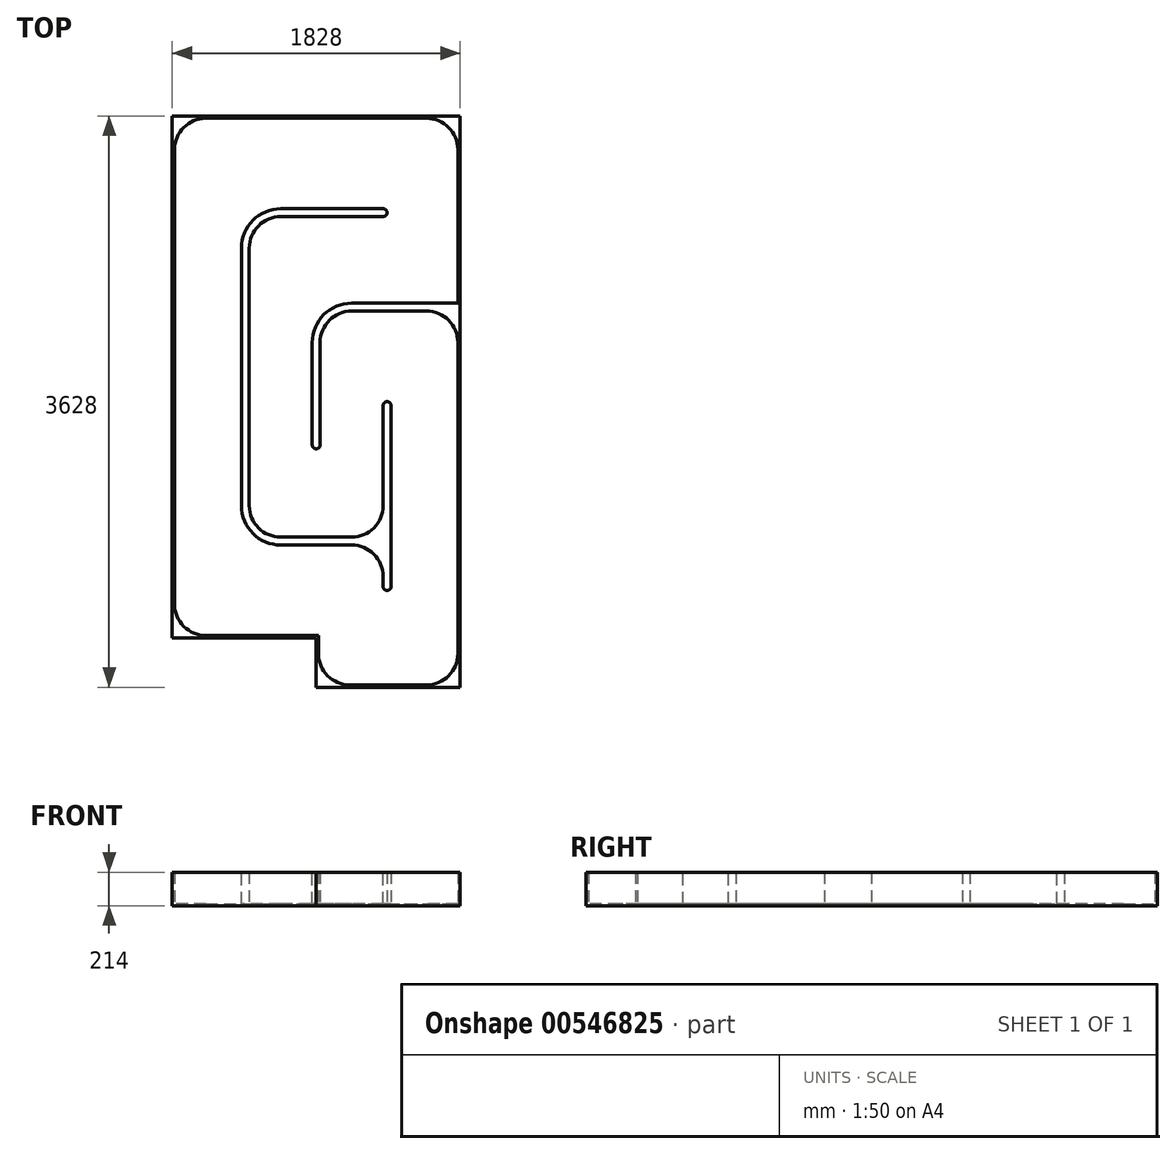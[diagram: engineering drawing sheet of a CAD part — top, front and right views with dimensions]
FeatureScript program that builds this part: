
annotation { "Feature Type Name" : "Feature", "Feature Type Description" : "" }
export const myFeature = defineFeature(function(context is Context, id is Id, definition is map)
    precondition{}
    {
        {
            assignVariable(context, id + "F0", {"name" : "H", "anyValue" : 200});
        }
        {
            assignVariable(context, id + "F1", {"name" : "t", "anyValue" : 14});
        }
        {
            assignVariable(context, id + "F2", {"name" : "w2", "anyValue" : 50});
        }
        {
            assignVariable(context, id + "F3", {"name" : "R1", "anyValue" : 200});
        }
        {
            assignVariable(context, id + "F4", {"name" : "R2", "anyValue" : getVariable(context, 'w2') / 2});
        }
        {
            var Q0;
            Q0=qCreatedBy(makeId("Top.planeOp"),FACE);
            var sketch = newSketch(context, id + "F5", { "sketchPlane" : qUnion([Q0])});
            skPoint(sketch, "E0.middle", {"position": v(0, 0) * mm});
            skLineSegment(sketch, "E1.bottom", {"start": v(-914, 1814) * mm, "end": v(914, 1814) * mm});
            skLineSegment(sketch, "E1.top", {"start": v(0, -1814) * mm, "end": v(914, -1814) * mm});
            skLineSegment(sketch, "E1.left", {"start": v(-914, 1814) * mm, "end": v(-914, -1500) * mm});
            skLineSegment(sketch, "E1.right", {"start": v(914, 1814) * mm, "end": v(914, -1814) * mm});
            skLineSegment(sketch, "E2", {"start": v(-914, -1500) * mm, "end": v(0, -1500) * mm});
            skLineSegment(sketch, "E3", {"start": v(0, -1500) * mm, "end": v(0, -1814) * mm});
            skPoint(sketch, "E4.orphan", {"position": v(-914, -1814) * mm});
            skPoint(sketch, "E5.orphan", {"position": v(914, -1814) * mm});
            skSolve(sketch);
        }
        {
            var Q0;
            Q0 = qSketchRegion(id + "F5", true);
            extrude(context, id + "F6", {"entities" : qUnion([Q0]), "depth" : (getVariable(context, 'H')) * mm, "offsetDistance" : 25 * mm, "hasSecondDirection" : true, "secondDirectionOppositeDirection" : true, "secondDirectionDepth" : (getVariable(context, 't')) * mm});
        }
        {
            var Q0;
            Q0=makeQuery(id+"F6.opExtrude","CAP_FACE",FACE,{"disambiguationData":[OSD([sQuery(id+"F5.wireOp",EDGE,"E1.bottom"),sQuery(id+"F5.wireOp",EDGE,"E1.top"),sQuery(id+"F5.wireOp",EDGE,"E1.left"),sQuery(id+"F5.wireOp",EDGE,"E1.right"),sQuery(id+"F5.wireOp",EDGE,"E2"),sQuery(id+"F5.wireOp",EDGE,"E3")])],"isStart":false});
            shell(context, id + "F7", {"entities" : qUnion([Q0]), "thickness" : (getVariable(context, 't')) * mm});
        }
        {
            var Q0;
            Q0=qCreatedBy(makeId("Top.planeOp"),FACE);
            var sketch = newSketch(context, id + "F8", { "sketchPlane" : qUnion([Q0])});
            skLineSegment(sketch, "E6", {"start": v(450, 1200) * mm, "end": v(-450, 1200) * mm});
            skLineSegment(sketch, "E7", {"start": v(-450, 1200) * mm, "end": v(-450, -886) * mm});
            skLineSegment(sketch, "E8", {"start": v(-450, -886) * mm, "end": v(450, -886) * mm});
            skLineSegment(sketch, "E9", {"start": v(450, -1200) * mm, "end": v(450, 0) * mm});
            skLineSegment(sketch, "E10", {"start": v(0, -300) * mm, "end": v(0, 600) * mm});
            skLineSegment(sketch, "E11", {"start": v(0, 600) * mm, "end": v(900, 600) * mm});
            skPoint(sketch, "E12.orphan", {"position": v(900, 1800) * mm});
            skSolve(sketch);
        }
        {
            var Q0;
            Q0=qCreatedBy(makeId("Right.planeOp"),FACE);
            var Q1;
            Q1=sQuery(id+"F8.wireOp",VERTEX,"E6.start");
            cPlane(context, id + "F9", {"entities" : qUnion([Q0, Q1]), "cplaneType" : CPlaneType.PLANE_POINT, "offset" : 25 * mm, "width" : 150 * mm, "height" : 150 * mm});
        }
        {
            var Q0;
            Q0=qCreatedBy(makeId("Front.planeOp"),FACE);
            var Q1;
            Q1=sQuery(id+"F8.wireOp",VERTEX,"E9.start");
            cPlane(context, id + "F10", {"entities" : qUnion([Q0, Q1]), "cplaneType" : CPlaneType.PLANE_POINT, "offset" : 25 * mm, "width" : 150 * mm, "height" : 150 * mm});
        }
        {
            var Q0;
            Q0=qCreatedBy(makeId("Front.planeOp"),FACE);
            var Q1;
            Q1=sQuery(id+"F8.wireOp",VERTEX,"E10.start");
            cPlane(context, id + "F11", {"entities" : qUnion([Q0, Q1]), "cplaneType" : CPlaneType.PLANE_POINT, "offset" : 25 * mm, "width" : 150 * mm, "height" : 150 * mm});
        }
        {
            var Q0;
            Q0=qCreatedBy(id+"F9.planeOp",FACE);
            var sketch = newSketch(context, id + "F12", { "sketchPlane" : qUnion([Q0])});
            skPoint(sketch, "E13.0", {"position": v(1200, 0) * mm});
            skLineSegment(sketch, "E14.bottom", {"start": v(1175, 200) * mm, "end": v(1225, 200) * mm});
            skLineSegment(sketch, "E14.top", {"start": v(1175, 0) * mm, "end": v(1225, 0) * mm});
            skLineSegment(sketch, "E14.left", {"start": v(1175, 200) * mm, "end": v(1175, 0) * mm});
            skLineSegment(sketch, "E14.right", {"start": v(1225, 200) * mm, "end": v(1225, 0) * mm});
            skSolve(sketch);
        }
        {
            var Q0;
            Q0=qCreatedBy(id+"F10.planeOp",FACE);
            var sketch = newSketch(context, id + "F13", { "sketchPlane" : qUnion([Q0])});
            skPoint(sketch, "E15.0", {"position": v(450, 0) * mm});
            skLineSegment(sketch, "E16.bottom", {"start": v(425, 200) * mm, "end": v(475, 200) * mm});
            skLineSegment(sketch, "E16.top", {"start": v(425, 0) * mm, "end": v(475, 0) * mm});
            skLineSegment(sketch, "E16.left", {"start": v(425, 200) * mm, "end": v(425, 0) * mm});
            skLineSegment(sketch, "E16.right", {"start": v(475, 200) * mm, "end": v(475, 0) * mm});
            skSolve(sketch);
        }
        {
            var Q0;
            Q0=qCreatedBy(id+"F11.planeOp",FACE);
            var sketch = newSketch(context, id + "F14", { "sketchPlane" : qUnion([Q0])});
            skLineSegment(sketch, "E17.bottom", {"start": v(-25, 200) * mm, "end": v(25, 200) * mm});
            skLineSegment(sketch, "E17.top", {"start": v(-25, 0) * mm, "end": v(25, 0) * mm});
            skLineSegment(sketch, "E17.left", {"start": v(-25, 200) * mm, "end": v(-25, 0) * mm});
            skLineSegment(sketch, "E17.right", {"start": v(25, 200) * mm, "end": v(25, 0) * mm});
            skSolve(sketch);
        }
        {
            var Q0;
            Q0 = qSketchRegion(id + "F12", true);
            var Q1;
            Q1=sQuery(id+"F8.wireOp",EDGE,"E6");
            var Q2;
            Q2=sQuery(id+"F8.wireOp",EDGE,"E7");
            var Q3;
            Q3=sQuery(id+"F8.wireOp",EDGE,"E8");
            sweep(context, id + "F15", {"profiles" : qUnion([Q0]), "path" : qUnion([Q1, Q2, Q3])});
        }
        {
            var Q0;
            Q0 = qSketchRegion(id + "F13", true);
            var Q1;
            Q1=sQuery(id+"F8.wireOp",EDGE,"E9");
            sweep(context, id + "F16", {"profiles" : qUnion([Q0]), "path" : qUnion([Q1])});
        }
        {
            var Q0;
            Q0 = qSketchRegion(id + "F14", true);
            var Q1;
            Q1=sQuery(id+"F8.wireOp",EDGE,"E10");
            var Q2;
            Q2=sQuery(id+"F8.wireOp",EDGE,"E11");
            sweep(context, id + "F17", {"operationType" : NewBodyOperationType.ADD, "profiles" : qUnion([Q0]), "path" : qUnion([Q1, Q2])});
        }
        {
            var Q0;
            Q0=makeQuery(id+"F15.opSweep","SWEPT_BODY",BODY,{"disambiguationData":[OSD([sQuery(id+"F8.wireOp",EDGE,"E8"),sQuery(id+"F12.wireOp",EDGE,"E14.bottom"),sQuery(id+"F12.wireOp",EDGE,"E14.top"),sQuery(id+"F12.wireOp",EDGE,"E14.left"),sQuery(id+"F12.wireOp",EDGE,"E14.right")])]});
            var Q1;
            Q1=makeQuery(id+"F16.opSweep","SWEPT_BODY",BODY,{"disambiguationData":[OSD([sQuery(id+"F8.wireOp",EDGE,"E9"),sQuery(id+"F13.wireOp",EDGE,"E16.bottom"),sQuery(id+"F13.wireOp",EDGE,"E16.top"),sQuery(id+"F13.wireOp",EDGE,"E16.left"),sQuery(id+"F13.wireOp",EDGE,"E16.right")])]});
            booleanBodies(context, id + "F18", {"operationType" : BooleanOperationType.UNION, "tools" : qUnion([Q0, Q1])});
        }
        {
            var Q0;
            Q0=makeQuery(id+"F18.opBoolean","INTERSECT",EDGE,{"derivedFrom":[makeQuery(id+"F15.opSweep","SWEPT_FACE",FACE,{"disambiguationData":[OSD([sQuery(id+"F8.wireOp",EDGE,"E8"),sQuery(id+"F12.wireOp",EDGE,"E14.right")])]}),makeQuery(id+"F16.opSweep","SWEPT_FACE",FACE,{"disambiguationData":[OSD([sQuery(id+"F8.wireOp",EDGE,"E9"),sQuery(id+"F13.wireOp",EDGE,"E16.left")])]})]});
            var Q1;
            Q1=makeQuery(id+"F18.opBoolean","INTERSECT",EDGE,{"derivedFrom":[makeQuery(id+"F15.opSweep","SWEPT_FACE",FACE,{"disambiguationData":[OSD([sQuery(id+"F8.wireOp",EDGE,"E8"),sQuery(id+"F12.wireOp",EDGE,"E14.left")])]}),makeQuery(id+"F16.opSweep","SWEPT_FACE",FACE,{"disambiguationData":[OSD([sQuery(id+"F8.wireOp",EDGE,"E9"),sQuery(id+"F13.wireOp",EDGE,"E16.left")])]})]});
            var Q2;
            Q2=makeQuery(id+"F15.opSweep","MID_CAP_EDGE",EDGE,{"disambiguationData":[OSD([sQuery(id+"F8.wireOp",VERTEX,"E8.start"),sQuery(id+"F12.wireOp",EDGE,"E14.left")])],"capPos":2.0});
            var Q3;
            Q3=makeQuery(id+"F15.opSweep","MID_CAP_EDGE",EDGE,{"disambiguationData":[OSD([sQuery(id+"F8.wireOp",VERTEX,"E7.start"),sQuery(id+"F12.wireOp",EDGE,"E14.left")])],"capPos":1.0});
            var Q4;
            Q4=makeQuery(id+"F17.opSweep","MID_CAP_EDGE",EDGE,{"disambiguationData":[OSD([sQuery(id+"F8.wireOp",VERTEX,"E11.start"),sQuery(id+"F14.wireOp",EDGE,"E17.right")])],"capPos":1.0});
            var Q5;
            Q5=makeQuery(id+"F17.opSweep","CAP_EDGE",EDGE,{"disambiguationData":[OSD([sQuery(id+"F8.wireOp",VERTEX,"E11.end"),sQuery(id+"F14.wireOp",EDGE,"E17.right")])],"isStart":false});
            var Q6;
            Q6=makeQuery(id+"F17.opSweep","CAP_EDGE",EDGE,{"disambiguationData":[OSD([sQuery(id+"F8.wireOp",VERTEX,"E11.end"),sQuery(id+"F14.wireOp",EDGE,"E17.left")])],"isStart":false});
            var Q7;
            Q7=makeQuery(id+"F7.opShell","OFFSET_EDGE",EDGE,{"disambiguationData":[OSD([sQuery(id+"F5.wireOp",EDGE,"E1.top"),sQuery(id+"F5.wireOp",EDGE,"E3")])]});
            var Q8;
            Q8=makeQuery(id+"F7.opShell","OFFSET_EDGE",EDGE,{"disambiguationData":[OSD([sQuery(id+"F5.wireOp",EDGE,"E1.top"),sQuery(id+"F5.wireOp",EDGE,"E1.right")])]});
            var Q9;
            Q9=makeQuery(id+"F7.opShell","OFFSET_EDGE",EDGE,{"disambiguationData":[OSD([sQuery(id+"F5.wireOp",EDGE,"E1.left"),sQuery(id+"F5.wireOp",EDGE,"E2")])]});
            var Q10;
            Q10=makeQuery(id+"F7.opShell","OFFSET_EDGE",EDGE,{"disambiguationData":[OSD([sQuery(id+"F5.wireOp",EDGE,"E1.bottom"),sQuery(id+"F5.wireOp",EDGE,"E1.left")])]});
            var Q11;
            Q11=makeQuery(id+"F7.opShell","OFFSET_EDGE",EDGE,{"disambiguationData":[OSD([sQuery(id+"F5.wireOp",EDGE,"E1.bottom"),sQuery(id+"F5.wireOp",EDGE,"E1.right")])]});
            fillet(context, id + "F19", {"entities" : qUnion([Q0, Q1, Q2, Q3, Q4, Q5, Q6, Q7, Q8, Q9, Q10, Q11]), "radius" : (getVariable(context, 'R1')) * mm, "tangentPropagation" : true, "allowEdgeOverflow" : false});
        }
        {
            var Q0;
            Q0=makeQuery(id+"F15.opSweep","MID_CAP_EDGE",EDGE,{"disambiguationData":[OSD([sQuery(id+"F8.wireOp",VERTEX,"E7.start"),sQuery(id+"F12.wireOp",EDGE,"E14.right")])],"capPos":1.0});
            var Q1;
            Q1=makeQuery(id+"F15.opSweep","MID_CAP_EDGE",EDGE,{"disambiguationData":[OSD([sQuery(id+"F8.wireOp",VERTEX,"E8.start"),sQuery(id+"F12.wireOp",EDGE,"E14.right")])],"capPos":2.0});
            var Q2;
            Q2=makeQuery(id+"F17.opSweep","MID_CAP_EDGE",EDGE,{"disambiguationData":[OSD([sQuery(id+"F8.wireOp",VERTEX,"E11.start"),sQuery(id+"F14.wireOp",EDGE,"E17.left")])],"capPos":1.0});
            fillet(context, id + "F20", {"entities" : qUnion([Q0, Q1, Q2]), "radius" : (getVariable(context, 'R1') + getVariable(context, 'w2')) * mm, "tangentPropagation" : true, "allowEdgeOverflow" : false});
        }
        {
            var Q0;
            Q0=makeQuery(id+"F15.opSweep","CAP_EDGE",EDGE,{"disambiguationData":[OSD([sQuery(id+"F8.wireOp",VERTEX,"E6.start"),sQuery(id+"F12.wireOp",EDGE,"E14.right")])],"isStart":true});
            var Q1;
            Q1=makeQuery(id+"F15.opSweep","CAP_EDGE",EDGE,{"disambiguationData":[OSD([sQuery(id+"F8.wireOp",VERTEX,"E6.start"),sQuery(id+"F12.wireOp",EDGE,"E14.left")])],"isStart":true});
            var Q2;
            Q2=makeQuery(id+"F17.opSweep","CAP_EDGE",EDGE,{"disambiguationData":[OSD([sQuery(id+"F8.wireOp",VERTEX,"E10.start"),sQuery(id+"F14.wireOp",EDGE,"E17.right")])],"isStart":true});
            var Q3;
            Q3=makeQuery(id+"F17.opSweep","CAP_EDGE",EDGE,{"disambiguationData":[OSD([sQuery(id+"F8.wireOp",VERTEX,"E10.start"),sQuery(id+"F14.wireOp",EDGE,"E17.left")])],"isStart":true});
            var Q4;
            Q4=makeQuery(id+"F16.opSweep","CAP_EDGE",EDGE,{"disambiguationData":[OSD([sQuery(id+"F8.wireOp",VERTEX,"E9.end"),sQuery(id+"F13.wireOp",EDGE,"E16.left")])],"isStart":false});
            var Q5;
            Q5=makeQuery(id+"F16.opSweep","CAP_EDGE",EDGE,{"disambiguationData":[OSD([sQuery(id+"F8.wireOp",VERTEX,"E9.end"),sQuery(id+"F13.wireOp",EDGE,"E16.right")])],"isStart":false});
            var Q6;
            Q6=makeQuery(id+"F16.opSweep","CAP_EDGE",EDGE,{"disambiguationData":[OSD([sQuery(id+"F8.wireOp",VERTEX,"E9.start"),sQuery(id+"F13.wireOp",EDGE,"E16.left")])],"isStart":true});
            var Q7;
            Q7=makeQuery(id+"F16.opSweep","CAP_EDGE",EDGE,{"disambiguationData":[OSD([sQuery(id+"F8.wireOp",VERTEX,"E9.start"),sQuery(id+"F13.wireOp",EDGE,"E16.right")])],"isStart":true});
            fillet(context, id + "F21", {"entities" : qUnion([Q0, Q1, Q2, Q3, Q4, Q5, Q6, Q7]), "radius" : (getVariable(context, 'R2')) * mm, "tangentPropagation" : true, "allowEdgeOverflow" : false});
        }
    });
